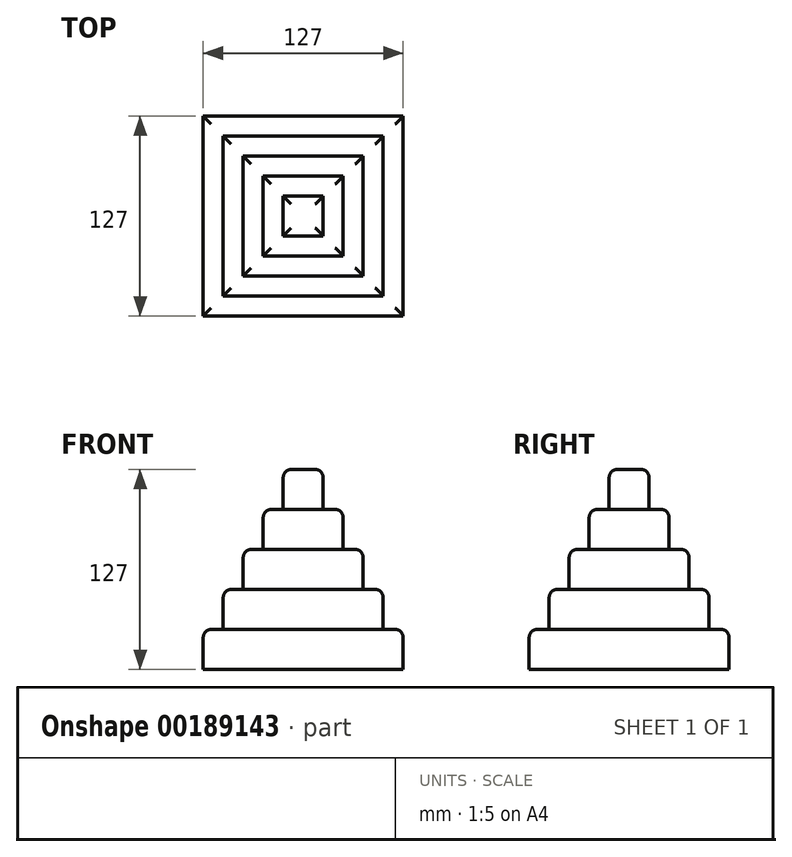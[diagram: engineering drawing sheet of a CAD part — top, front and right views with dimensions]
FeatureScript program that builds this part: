
annotation { "Feature Type Name" : "Feature", "Feature Type Description" : "" }
export const myFeature = defineFeature(function(context is Context, id is Id, definition is map)
    precondition{}
    {
        {
            var Q0;
            Q0=qCreatedBy(makeId("Top.planeOp"),FACE);
            var sketch = newSketch(context, id + "F0", { "sketchPlane" : qUnion([Q0])});
            skLineSegment(sketch, "E0.bottom", {"start": v(12.7, -12.7) * mm, "end": v(-12.7, -12.7) * mm});
            skLineSegment(sketch, "E0.top", {"start": v(12.7, 12.7) * mm, "end": v(-12.7, 12.7) * mm});
            skLineSegment(sketch, "E0.left", {"start": v(12.7, -12.7) * mm, "end": v(12.7, 12.7) * mm});
            skLineSegment(sketch, "E0.right", {"start": v(-12.7, -12.7) * mm, "end": v(-12.7, 12.7) * mm});
            skPoint(sketch, "E0.middle", {"position": v(0, 0) * mm});
            skSolve(sketch);
        }
        {
            var Q0;
            Q0=makeQuery(id+"F0.imprint","IMPRINT",FACE,{"disambiguationData":[TD([[makeQuery(id+"F0.imprint","IMPRINT",EDGE,{"derivedFrom":sQuery(id+"F0.wireOp",EDGE,"E0.bottom")}),-1.0]])]});
            extrude(context, id + "F1", {"entities" : qUnion([Q0]), "depth" : 127 * mm});
        }
        {
            var Q0;
            Q0=qCreatedBy(makeId("Top.planeOp"),FACE);
            var sketch = newSketch(context, id + "F2", { "sketchPlane" : qUnion([Q0])});
            skLineSegment(sketch, "E1.bottom", {"start": v(25.4, -25.4) * mm, "end": v(-25.4, -25.4) * mm});
            skLineSegment(sketch, "E1.top", {"start": v(25.4, 25.4) * mm, "end": v(-25.4, 25.4) * mm});
            skLineSegment(sketch, "E1.left", {"start": v(25.4, -25.4) * mm, "end": v(25.4, 25.4) * mm});
            skLineSegment(sketch, "E1.right", {"start": v(-25.4, -25.4) * mm, "end": v(-25.4, 25.4) * mm});
            skPoint(sketch, "E1.middle", {"position": v(0, 0) * mm});
            skSolve(sketch);
        }
        {
            var Q0;
            Q0=makeQuery(id+"F2.imprint","IMPRINT",FACE,{"disambiguationData":[TD([[makeQuery(id+"F2.imprint","IMPRINT",EDGE,{"derivedFrom":sQuery(id+"F2.wireOp",EDGE,"E1.bottom")}),-1.0]])]});
            extrude(context, id + "F3", {"entities" : qUnion([Q0]), "operationType" : NewBodyOperationType.ADD, "depth" : 101.6 * mm});
        }
        {
            var Q0;
            Q0=qCreatedBy(makeId("Top.planeOp"),FACE);
            var sketch = newSketch(context, id + "F4", { "sketchPlane" : qUnion([Q0])});
            skLineSegment(sketch, "E2.bottom", {"start": v(38.1, -38.1) * mm, "end": v(-38.1, -38.1) * mm});
            skLineSegment(sketch, "E2.top", {"start": v(38.1, 38.1) * mm, "end": v(-38.1, 38.1) * mm});
            skLineSegment(sketch, "E2.left", {"start": v(38.1, -38.1) * mm, "end": v(38.1, 38.1) * mm});
            skLineSegment(sketch, "E2.right", {"start": v(-38.1, -38.1) * mm, "end": v(-38.1, 38.1) * mm});
            skPoint(sketch, "E2.middle", {"position": v(0, 0) * mm});
            skSolve(sketch);
        }
        {
            var Q0;
            Q0=makeQuery(id+"F4.imprint","IMPRINT",FACE,{"disambiguationData":[TD([[makeQuery(id+"F4.imprint","IMPRINT",EDGE,{"derivedFrom":sQuery(id+"F4.wireOp",EDGE,"E2.bottom")}),-1.0]])]});
            extrude(context, id + "F5", {"entities" : qUnion([Q0]), "operationType" : NewBodyOperationType.ADD, "depth" : 76.2 * mm});
        }
        {
            var Q0;
            Q0=qCreatedBy(makeId("Top.planeOp"),FACE);
            var sketch = newSketch(context, id + "F6", { "sketchPlane" : qUnion([Q0])});
            skLineSegment(sketch, "E3.bottom", {"start": v(50.8, -50.8) * mm, "end": v(-50.8, -50.8) * mm});
            skLineSegment(sketch, "E3.top", {"start": v(50.8, 50.8) * mm, "end": v(-50.8, 50.8) * mm});
            skLineSegment(sketch, "E3.left", {"start": v(50.8, -50.8) * mm, "end": v(50.8, 50.8) * mm});
            skLineSegment(sketch, "E3.right", {"start": v(-50.8, -50.8) * mm, "end": v(-50.8, 50.8) * mm});
            skPoint(sketch, "E3.middle", {"position": v(0, 0) * mm});
            skSolve(sketch);
        }
        {
            var Q0;
            Q0=makeQuery(id+"F6.imprint","IMPRINT",FACE,{"disambiguationData":[TD([[makeQuery(id+"F6.imprint","IMPRINT",EDGE,{"derivedFrom":sQuery(id+"F6.wireOp",EDGE,"E3.bottom")}),-1.0]])]});
            extrude(context, id + "F7", {"entities" : qUnion([Q0]), "operationType" : NewBodyOperationType.ADD, "depth" : 50.8 * mm});
        }
        {
            var Q0;
            Q0=qCreatedBy(makeId("Top.planeOp"),FACE);
            var sketch = newSketch(context, id + "F8", { "sketchPlane" : qUnion([Q0])});
            skLineSegment(sketch, "E4.bottom", {"start": v(63.5, -63.5) * mm, "end": v(-63.5, -63.5) * mm});
            skLineSegment(sketch, "E4.top", {"start": v(63.5, 63.5) * mm, "end": v(-63.5, 63.5) * mm});
            skLineSegment(sketch, "E4.left", {"start": v(63.5, -63.5) * mm, "end": v(63.5, 63.5) * mm});
            skLineSegment(sketch, "E4.right", {"start": v(-63.5, -63.5) * mm, "end": v(-63.5, 63.5) * mm});
            skPoint(sketch, "E4.middle", {"position": v(0, 0) * mm});
            skSolve(sketch);
        }
        {
            var Q0;
            Q0=makeQuery(id+"F8.imprint","IMPRINT",FACE,{"disambiguationData":[TD([[makeQuery(id+"F8.imprint","IMPRINT",EDGE,{"derivedFrom":sQuery(id+"F8.wireOp",EDGE,"E4.bottom")}),-1.0]])]});
            extrude(context, id + "F9", {"entities" : qUnion([Q0]), "operationType" : NewBodyOperationType.ADD, "depth" : 25.4 * mm});
        }
        {
            var Q0;
            Q0=makeQuery(id+"F1.opExtrude","CAP_EDGE",EDGE,{"disambiguationData":[OSD([sQuery(id+"F0.wireOp",EDGE,"E0.bottom")])],"isStart":false});
            var Q1;
            Q1=makeQuery(id+"F3.opExtrude","CAP_EDGE",EDGE,{"disambiguationData":[OSD([sQuery(id+"F2.wireOp",EDGE,"E1.bottom")])],"isStart":false});
            var Q2;
            Q2=makeQuery(id+"F5.opExtrude","CAP_EDGE",EDGE,{"disambiguationData":[OSD([sQuery(id+"F4.wireOp",EDGE,"E2.bottom")])],"isStart":false});
            var Q3;
            Q3=makeQuery(id+"F7.opExtrude","CAP_EDGE",EDGE,{"disambiguationData":[OSD([sQuery(id+"F6.wireOp",EDGE,"E3.bottom")])],"isStart":false});
            var Q4;
            Q4=makeQuery(id+"F9.opExtrude","CAP_EDGE",EDGE,{"disambiguationData":[OSD([sQuery(id+"F8.wireOp",EDGE,"E4.bottom")])],"isStart":false});
            var Q5;
            Q5=makeQuery(id+"F1.opExtrude","CAP_EDGE",EDGE,{"disambiguationData":[OSD([sQuery(id+"F0.wireOp",EDGE,"E0.left")])],"isStart":false});
            var Q6;
            Q6=makeQuery(id+"F1.opExtrude","CAP_EDGE",EDGE,{"disambiguationData":[OSD([sQuery(id+"F0.wireOp",EDGE,"E0.top")])],"isStart":false});
            var Q7;
            Q7=makeQuery(id+"F1.opExtrude","CAP_EDGE",EDGE,{"disambiguationData":[OSD([sQuery(id+"F0.wireOp",EDGE,"E0.right")])],"isStart":false});
            var Q8;
            Q8=makeQuery(id+"F3.opExtrude","CAP_EDGE",EDGE,{"disambiguationData":[OSD([sQuery(id+"F2.wireOp",EDGE,"E1.left")])],"isStart":false});
            var Q9;
            Q9=makeQuery(id+"F3.opExtrude","CAP_EDGE",EDGE,{"disambiguationData":[OSD([sQuery(id+"F2.wireOp",EDGE,"E1.top")])],"isStart":false});
            var Q10;
            Q10=makeQuery(id+"F3.opExtrude","CAP_EDGE",EDGE,{"disambiguationData":[OSD([sQuery(id+"F2.wireOp",EDGE,"E1.right")])],"isStart":false});
            var Q11;
            Q11=makeQuery(id+"F5.opExtrude","CAP_EDGE",EDGE,{"disambiguationData":[OSD([sQuery(id+"F4.wireOp",EDGE,"E2.left")])],"isStart":false});
            var Q12;
            Q12=makeQuery(id+"F5.opExtrude","CAP_EDGE",EDGE,{"disambiguationData":[OSD([sQuery(id+"F4.wireOp",EDGE,"E2.top")])],"isStart":false});
            var Q13;
            Q13=makeQuery(id+"F5.opExtrude","CAP_EDGE",EDGE,{"disambiguationData":[OSD([sQuery(id+"F4.wireOp",EDGE,"E2.right")])],"isStart":false});
            var Q14;
            Q14=makeQuery(id+"F7.opExtrude","CAP_EDGE",EDGE,{"disambiguationData":[OSD([sQuery(id+"F6.wireOp",EDGE,"E3.right")])],"isStart":false});
            var Q15;
            Q15=makeQuery(id+"F9.opExtrude","CAP_EDGE",EDGE,{"disambiguationData":[OSD([sQuery(id+"F8.wireOp",EDGE,"E4.right")])],"isStart":false});
            var Q16;
            Q16=makeQuery(id+"F7.opExtrude","CAP_EDGE",EDGE,{"disambiguationData":[OSD([sQuery(id+"F6.wireOp",EDGE,"E3.left")])],"isStart":false});
            var Q17;
            Q17=makeQuery(id+"F9.opExtrude","CAP_EDGE",EDGE,{"disambiguationData":[OSD([sQuery(id+"F8.wireOp",EDGE,"E4.left")])],"isStart":false});
            var Q18;
            Q18=makeQuery(id+"F7.opExtrude","CAP_EDGE",EDGE,{"disambiguationData":[OSD([sQuery(id+"F6.wireOp",EDGE,"E3.top")])],"isStart":false});
            var Q19;
            Q19=makeQuery(id+"F9.opExtrude","CAP_EDGE",EDGE,{"disambiguationData":[OSD([sQuery(id+"F8.wireOp",EDGE,"E4.top")])],"isStart":false});
            fillet(context, id + "F10", {"entities" : qUnion([Q0, Q1, Q2, Q3, Q4, Q5, Q6, Q7, Q8, Q9, Q10, Q11, Q12, Q13, Q14, Q15, Q16, Q17, Q18, Q19]), "radius" : 5.08 * mm, "tangentPropagation" : true, "allowEdgeOverflow" : false});
        }
    });
